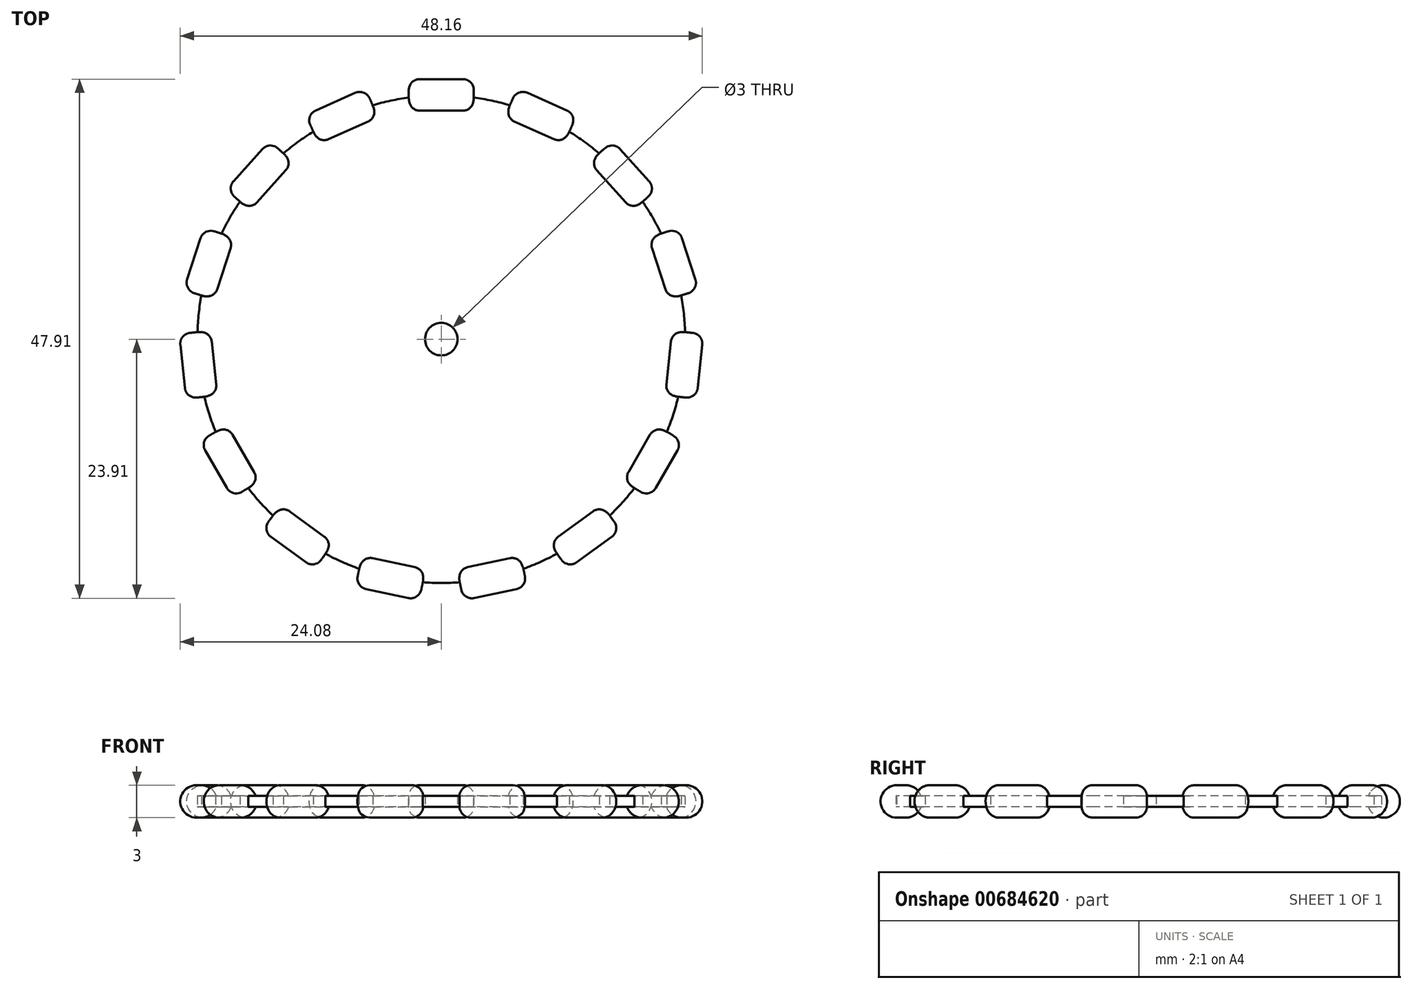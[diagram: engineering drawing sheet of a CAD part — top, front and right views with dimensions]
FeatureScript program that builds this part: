
annotation { "Feature Type Name" : "Feature", "Feature Type Description" : "" }
export const myFeature = defineFeature(function(context is Context, id is Id, definition is map)
    precondition{}
    {
        {
            var Q0;
            Q0=qCreatedBy(makeId("Top.planeOp"),FACE);
            var sketch = newSketch(context, id + "F0", { "sketchPlane" : qUnion([Q0])});
            skCircle(sketch, "E0", {"center": v(0, 0) * mm, "radius": 22.5 * mm, "construction": true});
            skPoint(sketch, "E1", {"position": v(0, 22.5) * mm});
            skSolve(sketch);
        }
        {
            var Q0;
            Q0=qCreatedBy(makeId("Right.planeOp"),FACE);
            var sketch = newSketch(context, id + "F1", { "sketchPlane" : qUnion([Q0])});
            skPoint(sketch, "E2.0", {"position": v(22.5, 0) * mm});
            skCircle(sketch, "E3", {"center": v(22.5, 0) * mm, "radius": 1.5 * mm});
            skSolve(sketch);
        }
        {
            var Q0;
            Q0 = qSketchRegion(id + "F1", true);
            extrude(context, id + "F2", {"entities" : qUnion([Q0]), "depth" : 3 * mm, "offsetDistance" : 25 * mm, "hasSecondDirection" : true, "secondDirectionOppositeDirection" : true, "secondDirectionDepth" : 3 * mm});
        }
        {
            var Q0;
            Q0=makeQuery(id+"F2.opExtrude","CAP_EDGE",EDGE,{"disambiguationData":[OSD([sQuery(id+"F1.wireOp",EDGE,"E3")])],"isStart":false});
            var Q1;
            Q1=makeQuery(id+"F2.opExtrude","CAP_FACE",FACE,{"disambiguationData":[OSD([sQuery(id+"F1.wireOp",EDGE,"E3")])],"isStart":true});
            fillet(context, id + "F3", {"entities" : qUnion([Q0, Q1]), "radius" : 1 * mm, "tangentPropagation" : true, "allowEdgeOverflow" : false});
        }
        {
            var Q0;
            Q0=makeQuery(id+"F2.opExtrude","SWEPT_BODY",BODY,{"disambiguationData":[OSD([sQuery(id+"F1.wireOp",EDGE,"E3")])]});
            var Q1;
            Q1=sQuery(id+"F0.wireOp",EDGE,"E0");
            circularPattern(context, id + "F4", {"entities" : qUnion([Q0]), "axis" : qUnion([Q1]), "angle" : 360 * degree, "instanceCount" : 15, "equalSpace" : true});
        }
        {
            var Q0;
            Q0=qCreatedBy(makeId("Top.planeOp"),FACE);
            var sketch = newSketch(context, id + "F5", { "sketchPlane" : qUnion([Q0])});
            skCircle(sketch, "E4.0", {"center": v(0, 0) * mm, "radius": 22.5 * mm});
            skCircle(sketch, "E5", {"center": v(0, 0) * mm, "radius": 1.5 * mm});
            skSolve(sketch);
        }
        {
            var Q0;
            Q0 = qSketchRegion(id + "F5", true);
            extrude(context, id + "F6", {"entities" : qUnion([Q0]), "operationType" : NewBodyOperationType.ADD, "depth" : 0.5 * mm, "offsetDistance" : 25 * mm, "hasSecondDirection" : true, "secondDirectionOppositeDirection" : true, "secondDirectionDepth" : 0.5 * mm});
        }
    });
